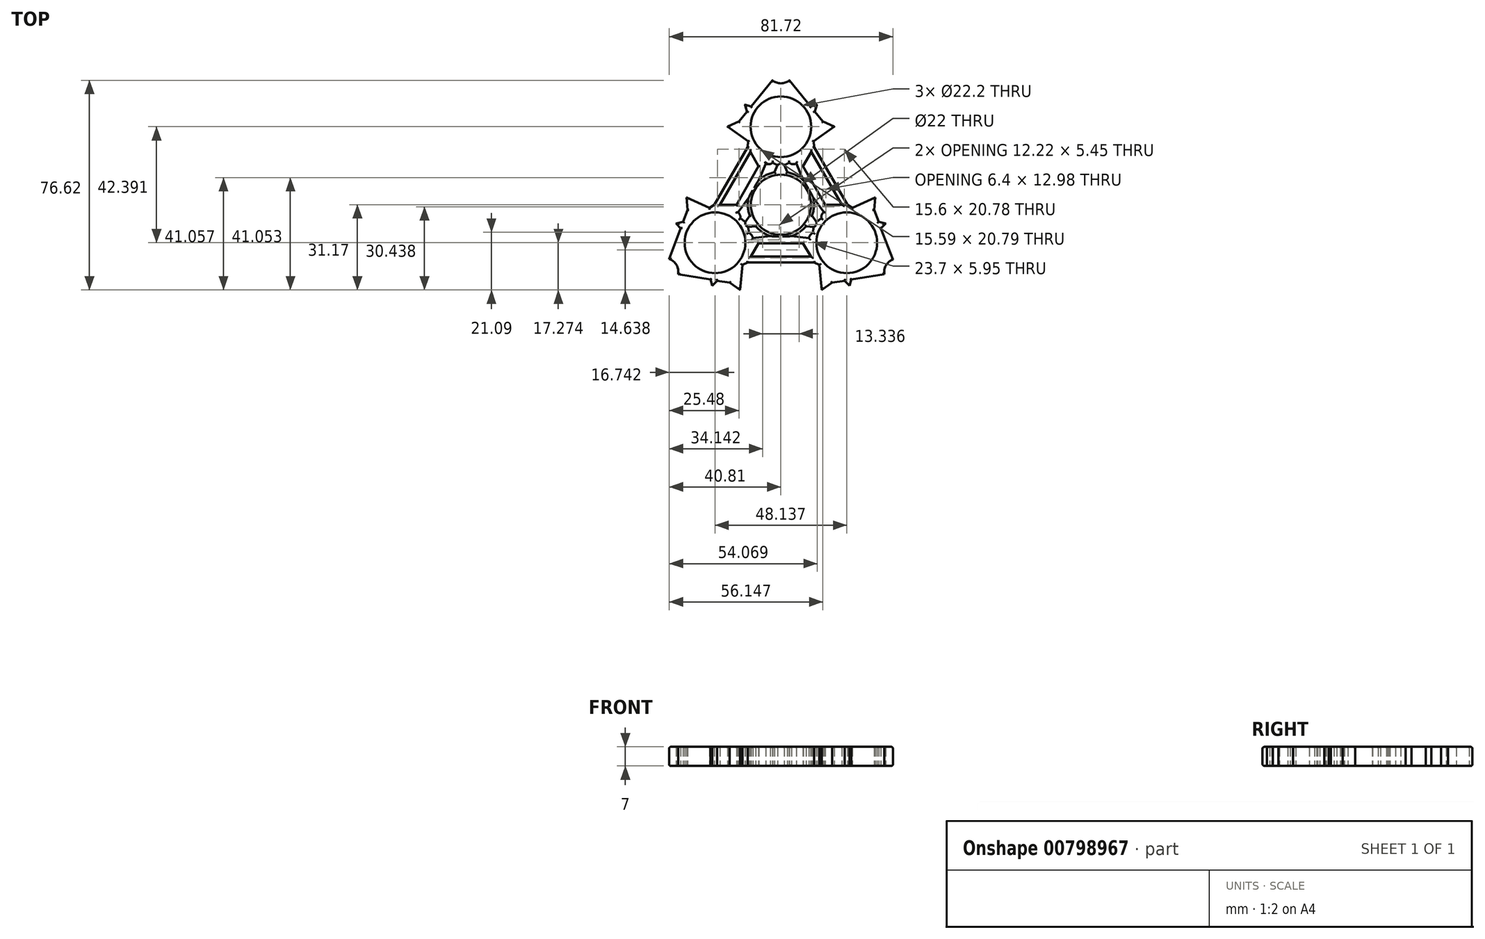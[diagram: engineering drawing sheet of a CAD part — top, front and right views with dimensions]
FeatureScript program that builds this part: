
annotation { "Feature Type Name" : "Feature", "Feature Type Description" : "" }
export const myFeature = defineFeature(function(context is Context, id is Id, definition is map)
    precondition{}
    {
        {
            var Q0;
            Q0=qCreatedBy(makeId("Top.planeOp"),FACE);
            var sketch = newSketch(context, id + "F0", { "sketchPlane" : qUnion([Q0])});
            skCircle(sketch, "E0", {"center": v(0, 0) * mm, "radius": 11 * mm});
            skLineSegment(sketch, "E1.0", {"start": v(8.12, -14.07) * mm, "end": v(-8.12, -14.07) * mm});
            skLineSegment(sketch, "E1.1", {"start": v(-16.24, 0) * mm, "end": v(-8.12, 14.07) * mm});
            skPoint(sketch, "E1.0.midPoint", {"position": v(0, -14.07) * mm});
            skLineSegment(sketch, "E2", {"start": v(-12.18, 21.1) * mm, "end": v(-8.12, 14.07) * mm});
            skLineSegment(sketch, "E3", {"start": v(12.18, 21.1) * mm, "end": v(8.12, 14.07) * mm});
            skLineSegment(sketch, "E4.trimOffspring", {"start": v(8.12, 14.07) * mm, "end": v(16.24, 0) * mm});
            skLineSegment(sketch, "E5", {"start": v(12.18, -21.1) * mm, "end": v(8.12, -14.07) * mm});
            skLineSegment(sketch, "E6", {"start": v(26.1, -1.21) * mm, "end": v(24.36, 0) * mm});
            skLineSegment(sketch, "E7", {"start": v(24.36, 0) * mm, "end": v(16.24, 0) * mm});
            skLineSegment(sketch, "E8", {"start": v(-14.1, -21.99) * mm, "end": v(-12.18, -21.1) * mm});
            skLineSegment(sketch, "E9", {"start": v(-26.1, -1.21) * mm, "end": v(-24.36, 0) * mm});
            skLineSegment(sketch, "E10", {"start": v(-24.36, 0) * mm, "end": v(-16.24, 0) * mm});
            skLineSegment(sketch, "E11", {"start": v(-12.18, -21.1) * mm, "end": v(-8.12, -14.07) * mm});
            skLineSegment(sketch, "E12.bottom", {"start": v(-12.18, -21.1) * mm, "end": v(12.18, -21.1) * mm});
            skLineSegment(sketch, "E12.top", {"start": v(-10.97, -19) * mm, "end": v(10.97, -19) * mm});
            skLineSegment(sketch, "E13", {"start": v(12.18, 21.1) * mm, "end": v(24.36, 0) * mm});
            skLineSegment(sketch, "E14", {"start": v(12.18, 21.1) * mm, "end": v(11.12, 19.26) * mm});
            skLineSegment(sketch, "E15", {"start": v(24.36, 0) * mm, "end": v(22.26, 0) * mm});
            skLineSegment(sketch, "E16", {"start": v(22.26, 0) * mm, "end": v(11.12, 19.26) * mm});
            skLineSegment(sketch, "E17", {"start": v(-12.18, 21.1) * mm, "end": v(-24.36, 0) * mm});
            skLineSegment(sketch, "E18", {"start": v(-24.36, 0) * mm, "end": v(-22.25, 0) * mm});
            skLineSegment(sketch, "E19", {"start": v(-22.25, 0) * mm, "end": v(-11.12, 19.27) * mm});
            skPoint(sketch, "E20.orphan", {"position": v(24.07, -13.9) * mm});
            skLineSegment(sketch, "E21.2", {"start": v(-19.54, 28.5) * mm, "end": v(-15.36, 30.44) * mm});
            skLineSegment(sketch, "E22.trimOffspring", {"start": v(-12, 23.2) * mm, "end": v(-19.54, 28.5) * mm});
            skLineSegment(sketch, "E23.trimOffspring", {"start": v(-12, 23.2) * mm, "end": v(-12.18, 21.1) * mm});
            skLineSegment(sketch, "E24", {"start": v(0, 0) * mm, "end": v(0, 11) * mm, "construction": true});
            skLineSegment(sketch, "E25.MirrorCS", {"start": v(12, 23.2) * mm, "end": v(19.54, 28.5) * mm});
            skLineSegment(sketch, "E26.MirrorCS", {"start": v(19.54, 28.5) * mm, "end": v(15.36, 30.44) * mm});
            skLineSegment(sketch, "E27.trimOffspring", {"start": v(12, 23.2) * mm, "end": v(12.18, 21.1) * mm});
            skLineSegment(sketch, "E28", {"start": v(-19.54, 28.5) * mm, "end": v(19.54, 28.5) * mm, "construction": true});
            skLineSegment(sketch, "E29", {"start": v(-15.36, 30.44) * mm, "end": v(-12.42, 34.04) * mm});
            skLineSegment(sketch, "E30", {"start": v(3.1, 45.45) * mm, "end": v(10.85, 35.97) * mm});
            skLineSegment(sketch, "E31.2", {"start": v(13.11, 36.58) * mm, "end": v(12.42, 34.04) * mm});
            skLineSegment(sketch, "E32.trimOffspring", {"start": v(12.42, 34.04) * mm, "end": v(15.36, 30.44) * mm});
            skLineSegment(sketch, "E33.trimOffspring", {"start": v(10.83, 35.98) * mm, "end": v(13.11, 36.58) * mm});
            skArc(sketch, "E34.trimOffspring", {"start": v(12.42, 34.04) * mm, "mid": v(12.43, 34.07) * mm, "end": v(12.44, 34.1) * mm, "construction": true});
            skLineSegment(sketch, "E35.MirrorCS", {"start": v(-10.83, 35.98) * mm, "end": v(-13.11, 36.58) * mm});
            skLineSegment(sketch, "E36.MirrorCS", {"start": v(-13.11, 36.58) * mm, "end": v(-12.42, 34.04) * mm});
            skLineSegment(sketch, "E37.trimOffspring", {"start": v(-10.83, 35.98) * mm, "end": v(-3.1, 45.45) * mm});
            skLineSegment(sketch, "E38", {"start": v(0, 0) * mm, "end": v(9.6, 5.54) * mm, "construction": true});
            skLineSegment(sketch, "E39.MirrorCS", {"start": v(26.1, -1.21) * mm, "end": v(34.45, 2.68) * mm});
            skLineSegment(sketch, "E40.MirrorCS", {"start": v(34.45, 2.68) * mm, "end": v(34.04, -1.91) * mm});
            skLineSegment(sketch, "E41.MirrorCS", {"start": v(35.69, -6.26) * mm, "end": v(34.04, -1.91) * mm});
            skLineSegment(sketch, "E42.MirrorCS", {"start": v(38.24, -6.93) * mm, "end": v(35.69, -6.26) * mm});
            skLineSegment(sketch, "E43.MirrorCS", {"start": v(36.58, -8.6) * mm, "end": v(38.24, -6.93) * mm});
            skLineSegment(sketch, "E44.MirrorCS", {"start": v(40.9, -20.05) * mm, "end": v(36.57, -8.6) * mm});
            skLineSegment(sketch, "E45", {"start": v(0, 0) * mm, "end": v(9.53, -5.5) * mm, "construction": true});
            skLineSegment(sketch, "E46", {"start": v(0, 0) * mm, "end": v(0, -11) * mm, "construction": true});
            skLineSegment(sketch, "E47", {"start": v(0, 0) * mm, "end": v(-9.53, -5.5) * mm, "construction": true});
            skLineSegment(sketch, "E48", {"start": v(0, 0) * mm, "end": v(-9.53, 5.5) * mm, "construction": true});
            skLineSegment(sketch, "E49.MirrorCS", {"start": v(25.74, -27.37) * mm, "end": v(25.13, -29.65) * mm});
            skLineSegment(sketch, "E50.MirrorCS", {"start": v(25.13, -29.65) * mm, "end": v(23.27, -27.78) * mm});
            skLineSegment(sketch, "E51.MirrorCS", {"start": v(14.9, -31.17) * mm, "end": v(18.68, -28.53) * mm});
            skLineSegment(sketch, "E52.MirrorCS", {"start": v(23.27, -27.78) * mm, "end": v(18.68, -28.53) * mm});
            skLineSegment(sketch, "E53.MirrorCS", {"start": v(14.1, -21.99) * mm, "end": v(14.9, -31.17) * mm});
            skLineSegment(sketch, "E54.MirrorCS", {"start": v(37.82, -25.4) * mm, "end": v(25.72, -27.38) * mm});
            skLineSegment(sketch, "E55.trimOffspring", {"start": v(14.1, -21.99) * mm, "end": v(12.18, -21.1) * mm});
            skLineSegment(sketch, "E56.MirrorCS", {"start": v(-14.1, -21.99) * mm, "end": v(-14.9, -31.17) * mm});
            skLineSegment(sketch, "E57.MirrorCS", {"start": v(-14.9, -31.17) * mm, "end": v(-18.68, -28.53) * mm});
            skLineSegment(sketch, "E58.MirrorCS", {"start": v(-23.27, -27.78) * mm, "end": v(-18.68, -28.53) * mm});
            skLineSegment(sketch, "E59.MirrorCS", {"start": v(-25.13, -29.65) * mm, "end": v(-23.27, -27.78) * mm});
            skLineSegment(sketch, "E60.MirrorCS", {"start": v(-25.74, -27.37) * mm, "end": v(-25.13, -29.65) * mm});
            skLineSegment(sketch, "E61.MirrorCS", {"start": v(-37.53, -25.45) * mm, "end": v(-25.72, -27.38) * mm});
            skLineSegment(sketch, "E62.MirrorCS", {"start": v(-36.58, -8.6) * mm, "end": v(-38.24, -6.93) * mm});
            skLineSegment(sketch, "E63.MirrorCS", {"start": v(-38.24, -6.93) * mm, "end": v(-35.69, -6.26) * mm});
            skLineSegment(sketch, "E64.MirrorCS", {"start": v(-35.69, -6.26) * mm, "end": v(-34.04, -1.91) * mm});
            skLineSegment(sketch, "E65.MirrorCS", {"start": v(-34.45, 2.68) * mm, "end": v(-34.04, -1.91) * mm});
            skLineSegment(sketch, "E66.MirrorCS", {"start": v(-26.1, -1.21) * mm, "end": v(-34.45, 2.68) * mm});
            skLineSegment(sketch, "E67.MirrorCS", {"start": v(-40.8, -19.78) * mm, "end": v(-36.57, -8.6) * mm});
            skCircle(sketch, "E68", {"center": v(0, 28.5) * mm, "radius": 11.1 * mm});
            skCircle(sketch, "E69", {"center": v(24.07, -13.9) * mm, "radius": 11.1 * mm});
            skCircle(sketch, "E70", {"center": v(-24.07, -13.9) * mm, "radius": 11.1 * mm});
            skLineSegment(sketch, "E71", {"start": v(-10.48, -6.05) * mm, "end": v(-14.46, -8.35) * mm, "construction": true});
            skLineSegment(sketch, "E72", {"start": v(14.46, -8.35) * mm, "end": v(10.48, -6.05) * mm, "construction": true});
            skLineSegment(sketch, "E73", {"start": v(0, 14.4) * mm, "end": v(0, 12.1) * mm, "construction": true});
            skLineSegment(sketch, "E74", {"start": v(-3.87, -11.47) * mm, "end": v(-10.24, -12.23) * mm});
            skLineSegment(sketch, "E75", {"start": v(3.87, -11.47) * mm, "end": v(10.24, -12.23) * mm});
            skLineSegment(sketch, "E76", {"start": v(-8.07, 9.02) * mm, "end": v(-5.58, 15.03) * mm});
            skLineSegment(sketch, "E77", {"start": v(0, 28.5) * mm, "end": v(4.28, 18.25) * mm});
            skLineSegment(sketch, "E78", {"start": v(1.2, 14.54) * mm, "end": v(2.3, 11.88) * mm});
            skCircle(sketch, "E79", {"center": v(0, 0) * mm, "radius": 12.1 * mm});
            skLineSegment(sketch, "E80.MirrorCS", {"start": v(-1.2, 14.54) * mm, "end": v(-2.3, 11.88) * mm});
            skLineSegment(sketch, "E81", {"start": v(-39.8, -17.13) * mm, "end": v(-40.8, -19.78) * mm});
            skArc(sketch, "E82", {"start": v(-37.53, -25.45) * mm, "mid": v(-38.16, -22.03) * mm, "end": v(-40.8, -19.78) * mm});
            skLineSegment(sketch, "E83", {"start": v(34.18, -26) * mm, "end": v(37.82, -25.4) * mm});
            skArc(sketch, "E84", {"start": v(40.9, -20.05) * mm, "mid": v(38.4, -22.18) * mm, "end": v(37.82, -25.4) * mm});
            skArc(sketch, "E85.MirrorC", {"start": v(3.1, 45.45) * mm, "mid": v(0, 44.35) * mm, "end": v(-3.1, 45.45) * mm});
            skPoint(sketch, "E86.orphan", {"position": v(38.4, -25.3) * mm});
            skPoint(sketch, "E87.orphan", {"position": v(7.8, -7.76) * mm});
            skPoint(sketch, "E88.orphan", {"position": v(0, -11) * mm});
            skLineSegment(sketch, "E89.trimOffspring", {"start": v(0, -12.1) * mm, "end": v(0, -41.68) * mm, "construction": true});
            skLineSegment(sketch, "E90.trimOffspring", {"start": v(10.48, -6.05) * mm, "end": v(12.47, -7.2) * mm, "construction": true});
            skPoint(sketch, "E91.orphan", {"position": v(10.62, -2.87) * mm});
            skLineSegment(sketch, "E92.trimOffspring", {"start": v(10.48, 6.05) * mm, "end": v(41.95, 24.22) * mm, "construction": true});
            skPoint(sketch, "E93.orphan", {"position": v(2.83, 10.63) * mm});
            skPoint(sketch, "E94.orphan", {"position": v(-2.83, 10.63) * mm});
            skLineSegment(sketch, "E95.trimOffspring", {"start": v(0, 12.1) * mm, "end": v(0, 44.35) * mm, "construction": true});
            skPoint(sketch, "E96.orphan", {"position": v(-7.8, -7.76) * mm});
            skLineSegment(sketch, "E97.trimOffspring", {"start": v(-10.48, -6.05) * mm, "end": v(-38.16, -22.03) * mm, "construction": true});
            skPoint(sketch, "E98.orphan", {"position": v(-10.62, -2.87) * mm});
            skLineSegment(sketch, "E99.trimOffspring", {"start": v(-10.48, 6.05) * mm, "end": v(-49.35, 28.5) * mm, "construction": true});
            skPoint(sketch, "E100.MirrorCS.start.orphan", {"position": v(15.06, -8.7) * mm});
            skLineSegment(sketch, "E101", {"start": v(13.07, -6.36) * mm, "end": v(11.42, -4) * mm});
            skLineSegment(sketch, "E102", {"start": v(9.18, -7.88) * mm, "end": v(12.05, -8.14) * mm});
            skPoint(sketch, "E103.MirrorCS.start.orphan", {"position": v(-15.06, -8.7) * mm});
            skLineSegment(sketch, "E104", {"start": v(-13.07, -6.36) * mm, "end": v(-11.42, -4) * mm});
            skLineSegment(sketch, "E105", {"start": v(-12.05, -8.14) * mm, "end": v(-9.18, -7.88) * mm});
            skLineSegment(sketch, "E106", {"start": v(21.25, -12.27) * mm, "end": v(14.46, -8.35) * mm, "construction": true});
            skLineSegment(sketch, "E107", {"start": v(14.46, -8.35) * mm, "end": v(15.06, -8.7) * mm, "construction": true});
            skPoint(sketch, "E108.orphan", {"position": v(19.26, -11.12) * mm});
            skPoint(sketch, "E109.start.orphan", {"position": v(12.47, -7.2) * mm});
            skLineSegment(sketch, "E110.trimOffspring", {"start": v(14.46, -8.35) * mm, "end": v(19.26, -11.12) * mm, "construction": true});
            skLineSegment(sketch, "E111.trimOffspring", {"start": v(15.75, -2.72) * mm, "end": v(11.83, 2.53) * mm});
            skArc(sketch, "E112", {"start": v(11.81, -10.26) * mm, "mid": v(10.75, -11.02) * mm, "end": v(10.24, -12.23) * mm});
            skArc(sketch, "E113.MirrorCS", {"start": v(14.8, -5.1) * mm, "mid": v(14.92, -3.8) * mm, "end": v(15.71, -2.75) * mm});
            skLineSegment(sketch, "E114", {"start": v(15.71, -2.75) * mm, "end": v(15.75, -2.72) * mm});
            skArc(sketch, "E115.trimOffspring", {"start": v(14.8, -5.1) * mm, "mid": v(12.47, -7.2) * mm, "end": v(11.81, -10.26) * mm});
            skLineSegment(sketch, "E116.trimOffspring", {"start": v(24.07, -13.9) * mm, "end": v(38.4, -22.18) * mm, "construction": true});
            skArc(sketch, "E117.MirrorCS", {"start": v(-11.81, -10.26) * mm, "mid": v(-10.75, -11.02) * mm, "end": v(-10.24, -12.23) * mm});
            skArc(sketch, "E118.MirrorCS", {"start": v(-14.8, -5.1) * mm, "mid": v(-14.92, -3.8) * mm, "end": v(-15.71, -2.75) * mm});
            skArc(sketch, "E119.MirrorCS", {"start": v(-14.8, -5.1) * mm, "mid": v(-12.47, -7.2) * mm, "end": v(-11.81, -10.26) * mm});
            skLineSegment(sketch, "E120.trimOffspring", {"start": v(-15.71, -2.75) * mm, "end": v(-11.86, 2.38) * mm});
            skArc(sketch, "E121.MirrorCS", {"start": v(-2.98, 15.36) * mm, "mid": v(-4.17, 14.82) * mm, "end": v(-5.47, 14.98) * mm});
            skArc(sketch, "E122.MirrorCS", {"start": v(2.98, 15.36) * mm, "mid": v(0, 14.4) * mm, "end": v(-2.98, 15.36) * mm});
            skArc(sketch, "E123.MirrorCS", {"start": v(2.98, 15.36) * mm, "mid": v(4.17, 14.82) * mm, "end": v(5.47, 14.98) * mm});
            skLineSegment(sketch, "E124", {"start": v(-5.47, 14.98) * mm, "end": v(-5.58, 15.03) * mm});
            skLineSegment(sketch, "E125.trimOffspring", {"start": v(-4.25, 18.24) * mm, "end": v(0, 28.5) * mm});
            skPoint(sketch, "E126.orphan", {"position": v(0, 17.4) * mm});
            skLineSegment(sketch, "E127", {"start": v(5.47, 14.98) * mm, "end": v(5.62, 15.04) * mm});
            skLineSegment(sketch, "E128.trimOffspring", {"start": v(5.62, 15.04) * mm, "end": v(8.18, 8.92) * mm});
            skLineSegment(sketch, "E129", {"start": v(0, 0) * mm, "end": v(-38.16, -22.03) * mm, "construction": true});
            skSolve(sketch);
        }
        {
            var Q0;
            Q0 = qSketchRegion(id + "F0", true);
            var Q1;
            Q1=makeQuery(id+"F0.imprint","IMPRINT",FACE,{"disambiguationData":[TD([[makeQuery(id+"F0.imprint","IMPRINT",EDGE,{"derivedFrom":sQuery(id+"F0.wireOp",EDGE,"E0")}),-1.0]])]});
            var Q2;
            {var subQ0=sQuery(id+"F0.wireOp",EDGE,"E101");Q2=makeQuery(id+"F0.imprint","IMPRINT",FACE,{"disambiguationData":[TD([[makeQuery(id+"F0.imprint","IMPRINT",EDGE,{"derivedFrom":subQ0}),1.0]])]});}
            var Q3;
            {var subQ0=sQuery(id+"F0.wireOp",EDGE,"E104");Q3=makeQuery(id+"F0.imprint","IMPRINT",FACE,{"disambiguationData":[TD([[makeQuery(id+"F0.imprint","IMPRINT",EDGE,{"derivedFrom":subQ0}),-1.0]])]});}
            var Q4;
            {var subQ0=sQuery(id+"F0.wireOp",EDGE,"E78");Q4=makeQuery(id+"F0.imprint","IMPRINT",FACE,{"disambiguationData":[TD([[makeQuery(id+"F0.imprint","IMPRINT",EDGE,{"derivedFrom":subQ0}),-1.0]])]});}
            extrude(context, id + "F1", {"entities" : qUnion([Q0, Q1, Q2, Q3, Q4]), "depth" : 7 * mm, "offsetDistance" : 25.4 * mm});
        }
        {
            var Q0;
            Q0=makeQuery(id+"F1.opExtrude","CAP_FACE",FACE,{"disambiguationData":[OSD([sQuery(id+"F0.wireOp",EDGE,"E0"),sQuery(id+"F0.wireOp",EDGE,"E1.0"),sQuery(id+"F0.wireOp",EDGE,"E1.1"),sQuery(id+"F0.wireOp",EDGE,"E2"),sQuery(id+"F0.wireOp",EDGE,"E3"),sQuery(id+"F0.wireOp",EDGE,"E4.trimOffspring"),sQuery(id+"F0.wireOp",EDGE,"E5"),sQuery(id+"F0.wireOp",EDGE,"E6"),sQuery(id+"F0.wireOp",EDGE,"E7"),sQuery(id+"F0.wireOp",EDGE,"E8"),sQuery(id+"F0.wireOp",EDGE,"E9"),sQuery(id+"F0.wireOp",EDGE,"E10"),sQuery(id+"F0.wireOp",EDGE,"E11"),sQuery(id+"F0.wireOp",EDGE,"E12.bottom"),sQuery(id+"F0.wireOp",EDGE,"E12.top"),sQuery(id+"F0.wireOp",EDGE,"E13"),sQuery(id+"F0.wireOp",EDGE,"E16"),sQuery(id+"F0.wireOp",EDGE,"E17"),sQuery(id+"F0.wireOp",EDGE,"E19"),sQuery(id+"F0.wireOp",EDGE,"E21.2"),sQuery(id+"F0.wireOp",EDGE,"E22.trimOffspring"),sQuery(id+"F0.wireOp",EDGE,"E23.trimOffspring"),sQuery(id+"F0.wireOp",EDGE,"E25.MirrorCS"),sQuery(id+"F0.wireOp",EDGE,"E26.MirrorCS"),sQuery(id+"F0.wireOp",EDGE,"E27.trimOffspring"),sQuery(id+"F0.wireOp",EDGE,"E29"),sQuery(id+"F0.wireOp",EDGE,"E30"),sQuery(id+"F0.wireOp",EDGE,"E31.2"),sQuery(id+"F0.wireOp",EDGE,"E32.trimOffspring"),sQuery(id+"F0.wireOp",EDGE,"E33.trimOffspring"),sQuery(id+"F0.wireOp",EDGE,"E35.MirrorCS"),sQuery(id+"F0.wireOp",EDGE,"E36.MirrorCS"),sQuery(id+"F0.wireOp",EDGE,"E37.trimOffspring"),sQuery(id+"F0.wireOp",EDGE,"E39.MirrorCS"),sQuery(id+"F0.wireOp",EDGE,"E40.MirrorCS"),sQuery(id+"F0.wireOp",EDGE,"E41.MirrorCS"),sQuery(id+"F0.wireOp",EDGE,"E42.MirrorCS"),sQuery(id+"F0.wireOp",EDGE,"E43.MirrorCS"),sQuery(id+"F0.wireOp",EDGE,"E44.MirrorCS"),sQuery(id+"F0.wireOp",EDGE,"E49.MirrorCS"),sQuery(id+"F0.wireOp",EDGE,"E50.MirrorCS"),sQuery(id+"F0.wireOp",EDGE,"E51.MirrorCS"),sQuery(id+"F0.wireOp",EDGE,"E52.MirrorCS"),sQuery(id+"F0.wireOp",EDGE,"E53.MirrorCS"),sQuery(id+"F0.wireOp",EDGE,"E54.MirrorCS"),sQuery(id+"F0.wireOp",EDGE,"E55.trimOffspring"),sQuery(id+"F0.wireOp",EDGE,"E56.MirrorCS"),sQuery(id+"F0.wireOp",EDGE,"E57.MirrorCS"),sQuery(id+"F0.wireOp",EDGE,"E58.MirrorCS"),sQuery(id+"F0.wireOp",EDGE,"E59.MirrorCS"),sQuery(id+"F0.wireOp",EDGE,"E60.MirrorCS"),sQuery(id+"F0.wireOp",EDGE,"E61.MirrorCS"),sQuery(id+"F0.wireOp",EDGE,"E62.MirrorCS"),sQuery(id+"F0.wireOp",EDGE,"E63.MirrorCS"),sQuery(id+"F0.wireOp",EDGE,"E64.MirrorCS"),sQuery(id+"F0.wireOp",EDGE,"E65.MirrorCS"),sQuery(id+"F0.wireOp",EDGE,"E66.MirrorCS"),sQuery(id+"F0.wireOp",EDGE,"E67.MirrorCS"),sQuery(id+"F0.wireOp",EDGE,"E68"),sQuery(id+"F0.wireOp",EDGE,"E69"),sQuery(id+"F0.wireOp",EDGE,"E70"),sQuery(id+"F0.wireOp",EDGE,"E74"),sQuery(id+"F0.wireOp",EDGE,"E75"),sQuery(id+"F0.wireOp",EDGE,"E76"),sQuery(id+"F0.wireOp",EDGE,"E78"),sQuery(id+"F0.wireOp",EDGE,"E79"),sQuery(id+"F0.wireOp",EDGE,"E80.MirrorCS"),sQuery(id+"F0.wireOp",EDGE,"E81"),sQuery(id+"F0.wireOp",EDGE,"E82"),sQuery(id+"F0.wireOp",EDGE,"E83"),sQuery(id+"F0.wireOp",EDGE,"E84"),sQuery(id+"F0.wireOp",EDGE,"E85.MirrorC"),sQuery(id+"F0.wireOp",EDGE,"E101"),sQuery(id+"F0.wireOp",EDGE,"E102"),sQuery(id+"F0.wireOp",EDGE,"E104"),sQuery(id+"F0.wireOp",EDGE,"E105"),sQuery(id+"F0.wireOp",EDGE,"E111.trimOffspring"),sQuery(id+"F0.wireOp",EDGE,"E112"),sQuery(id+"F0.wireOp",EDGE,"E113.MirrorCS"),sQuery(id+"F0.wireOp",EDGE,"E114"),sQuery(id+"F0.wireOp",EDGE,"E115.trimOffspring"),sQuery(id+"F0.wireOp",EDGE,"E117.MirrorCS"),sQuery(id+"F0.wireOp",EDGE,"E118.MirrorCS"),sQuery(id+"F0.wireOp",EDGE,"E119.MirrorCS"),sQuery(id+"F0.wireOp",EDGE,"E120.trimOffspring"),sQuery(id+"F0.wireOp",EDGE,"E121.MirrorCS"),sQuery(id+"F0.wireOp",EDGE,"E122.MirrorCS"),sQuery(id+"F0.wireOp",EDGE,"E123.MirrorCS"),sQuery(id+"F0.wireOp",EDGE,"E124"),sQuery(id+"F0.wireOp",EDGE,"E127"),sQuery(id+"F0.wireOp",EDGE,"E128.trimOffspring")])],"isStart":false});
            fillet(context, id + "F2", {"entities" : qUnion([Q0]), "radius" : 0.5 * mm, "tangentPropagation" : true, "allowEdgeOverflow" : false});
        }
        {
            var Q0;
            Q0=makeQuery(id+"F1.opExtrude","CAP_FACE",FACE,{"disambiguationData":[OSD([sQuery(id+"F0.wireOp",EDGE,"E0"),sQuery(id+"F0.wireOp",EDGE,"E1.0"),sQuery(id+"F0.wireOp",EDGE,"E1.1"),sQuery(id+"F0.wireOp",EDGE,"E2"),sQuery(id+"F0.wireOp",EDGE,"E3"),sQuery(id+"F0.wireOp",EDGE,"E4.trimOffspring"),sQuery(id+"F0.wireOp",EDGE,"E5"),sQuery(id+"F0.wireOp",EDGE,"E6"),sQuery(id+"F0.wireOp",EDGE,"E7"),sQuery(id+"F0.wireOp",EDGE,"E8"),sQuery(id+"F0.wireOp",EDGE,"E9"),sQuery(id+"F0.wireOp",EDGE,"E10"),sQuery(id+"F0.wireOp",EDGE,"E11"),sQuery(id+"F0.wireOp",EDGE,"E12.bottom"),sQuery(id+"F0.wireOp",EDGE,"E12.top"),sQuery(id+"F0.wireOp",EDGE,"E13"),sQuery(id+"F0.wireOp",EDGE,"E16"),sQuery(id+"F0.wireOp",EDGE,"E17"),sQuery(id+"F0.wireOp",EDGE,"E19"),sQuery(id+"F0.wireOp",EDGE,"E21.2"),sQuery(id+"F0.wireOp",EDGE,"E22.trimOffspring"),sQuery(id+"F0.wireOp",EDGE,"E23.trimOffspring"),sQuery(id+"F0.wireOp",EDGE,"E25.MirrorCS"),sQuery(id+"F0.wireOp",EDGE,"E26.MirrorCS"),sQuery(id+"F0.wireOp",EDGE,"E27.trimOffspring"),sQuery(id+"F0.wireOp",EDGE,"E29"),sQuery(id+"F0.wireOp",EDGE,"E30"),sQuery(id+"F0.wireOp",EDGE,"E31.2"),sQuery(id+"F0.wireOp",EDGE,"E32.trimOffspring"),sQuery(id+"F0.wireOp",EDGE,"E33.trimOffspring"),sQuery(id+"F0.wireOp",EDGE,"E35.MirrorCS"),sQuery(id+"F0.wireOp",EDGE,"E36.MirrorCS"),sQuery(id+"F0.wireOp",EDGE,"E37.trimOffspring"),sQuery(id+"F0.wireOp",EDGE,"E39.MirrorCS"),sQuery(id+"F0.wireOp",EDGE,"E40.MirrorCS"),sQuery(id+"F0.wireOp",EDGE,"E41.MirrorCS"),sQuery(id+"F0.wireOp",EDGE,"E42.MirrorCS"),sQuery(id+"F0.wireOp",EDGE,"E43.MirrorCS"),sQuery(id+"F0.wireOp",EDGE,"E44.MirrorCS"),sQuery(id+"F0.wireOp",EDGE,"E49.MirrorCS"),sQuery(id+"F0.wireOp",EDGE,"E50.MirrorCS"),sQuery(id+"F0.wireOp",EDGE,"E51.MirrorCS"),sQuery(id+"F0.wireOp",EDGE,"E52.MirrorCS"),sQuery(id+"F0.wireOp",EDGE,"E53.MirrorCS"),sQuery(id+"F0.wireOp",EDGE,"E54.MirrorCS"),sQuery(id+"F0.wireOp",EDGE,"E55.trimOffspring"),sQuery(id+"F0.wireOp",EDGE,"E56.MirrorCS"),sQuery(id+"F0.wireOp",EDGE,"E57.MirrorCS"),sQuery(id+"F0.wireOp",EDGE,"E58.MirrorCS"),sQuery(id+"F0.wireOp",EDGE,"E59.MirrorCS"),sQuery(id+"F0.wireOp",EDGE,"E60.MirrorCS"),sQuery(id+"F0.wireOp",EDGE,"E61.MirrorCS"),sQuery(id+"F0.wireOp",EDGE,"E62.MirrorCS"),sQuery(id+"F0.wireOp",EDGE,"E63.MirrorCS"),sQuery(id+"F0.wireOp",EDGE,"E64.MirrorCS"),sQuery(id+"F0.wireOp",EDGE,"E65.MirrorCS"),sQuery(id+"F0.wireOp",EDGE,"E66.MirrorCS"),sQuery(id+"F0.wireOp",EDGE,"E67.MirrorCS"),sQuery(id+"F0.wireOp",EDGE,"E68"),sQuery(id+"F0.wireOp",EDGE,"E69"),sQuery(id+"F0.wireOp",EDGE,"E70"),sQuery(id+"F0.wireOp",EDGE,"E74"),sQuery(id+"F0.wireOp",EDGE,"E75"),sQuery(id+"F0.wireOp",EDGE,"E76"),sQuery(id+"F0.wireOp",EDGE,"E78"),sQuery(id+"F0.wireOp",EDGE,"E79"),sQuery(id+"F0.wireOp",EDGE,"E80.MirrorCS"),sQuery(id+"F0.wireOp",EDGE,"E81"),sQuery(id+"F0.wireOp",EDGE,"E82"),sQuery(id+"F0.wireOp",EDGE,"E83"),sQuery(id+"F0.wireOp",EDGE,"E84"),sQuery(id+"F0.wireOp",EDGE,"E85.MirrorC"),sQuery(id+"F0.wireOp",EDGE,"E101"),sQuery(id+"F0.wireOp",EDGE,"E102"),sQuery(id+"F0.wireOp",EDGE,"E104"),sQuery(id+"F0.wireOp",EDGE,"E105"),sQuery(id+"F0.wireOp",EDGE,"E111.trimOffspring"),sQuery(id+"F0.wireOp",EDGE,"E112"),sQuery(id+"F0.wireOp",EDGE,"E113.MirrorCS"),sQuery(id+"F0.wireOp",EDGE,"E114"),sQuery(id+"F0.wireOp",EDGE,"E115.trimOffspring"),sQuery(id+"F0.wireOp",EDGE,"E117.MirrorCS"),sQuery(id+"F0.wireOp",EDGE,"E118.MirrorCS"),sQuery(id+"F0.wireOp",EDGE,"E119.MirrorCS"),sQuery(id+"F0.wireOp",EDGE,"E120.trimOffspring"),sQuery(id+"F0.wireOp",EDGE,"E121.MirrorCS"),sQuery(id+"F0.wireOp",EDGE,"E122.MirrorCS"),sQuery(id+"F0.wireOp",EDGE,"E123.MirrorCS"),sQuery(id+"F0.wireOp",EDGE,"E124"),sQuery(id+"F0.wireOp",EDGE,"E127"),sQuery(id+"F0.wireOp",EDGE,"E128.trimOffspring")])],"isStart":true});
            fillet(context, id + "F3", {"entities" : qUnion([Q0]), "radius" : 0.5 * mm, "tangentPropagation" : true, "allowEdgeOverflow" : false});
        }
    });
